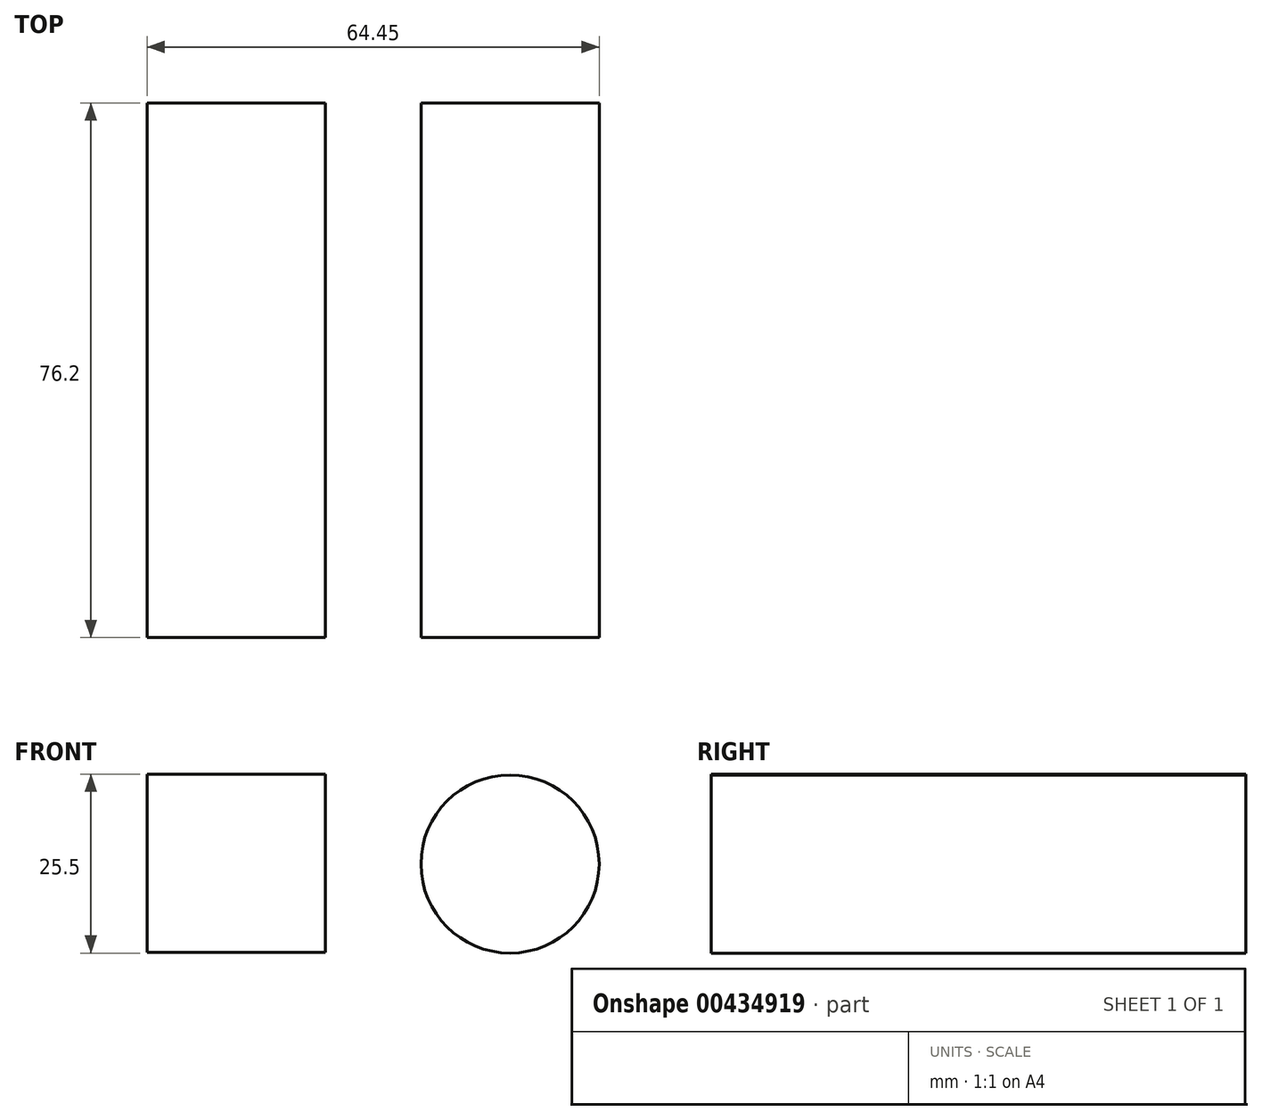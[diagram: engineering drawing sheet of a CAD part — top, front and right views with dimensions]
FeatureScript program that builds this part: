
annotation { "Feature Type Name" : "Feature", "Feature Type Description" : "" }
export const myFeature = defineFeature(function(context is Context, id is Id, definition is map)
    precondition{}
    {
        {
            var Q0;
            Q0=qCreatedBy(makeId("Front.planeOp"),FACE);
            var sketch = newSketch(context, id + "F0", { "sketchPlane" : qUnion([Q0])});
            skLineSegment(sketch, "E0", {"start": v(0, 0) * mm, "end": v(0, 25.4) * mm});
            skLineSegment(sketch, "E1", {"start": v(0, 25.4) * mm, "end": v(-25.4, 25.4) * mm});
            skLineSegment(sketch, "E2", {"start": v(-25.4, 25.4) * mm, "end": v(-25.4, 0) * mm});
            skLineSegment(sketch, "E3", {"start": v(-25.4, 0) * mm, "end": v(0, 0) * mm});
            skSolve(sketch);
        }
        {
            var Q0;
            Q0 = qSketchRegion(id + "F0", true);
            extrude(context, id + "F1", {"entities" : qUnion([Q0]), "depth" : 76.2 * mm});
        }
        {
            var Q0;
            Q0=qCreatedBy(makeId("Front.planeOp"),FACE);
            var sketch = newSketch(context, id + "F2", { "sketchPlane" : qUnion([Q0])});
            skCircle(sketch, "E4", {"center": v(26.35, 12.6) * mm, "radius": 12.7 * mm});
            skSolve(sketch);
        }
        {
            var Q0;
            Q0 = qSketchRegion(id + "F2", true);
            extrude(context, id + "F3", {"entities" : qUnion([Q0]), "depth" : 76.2 * mm});
        }
    });
